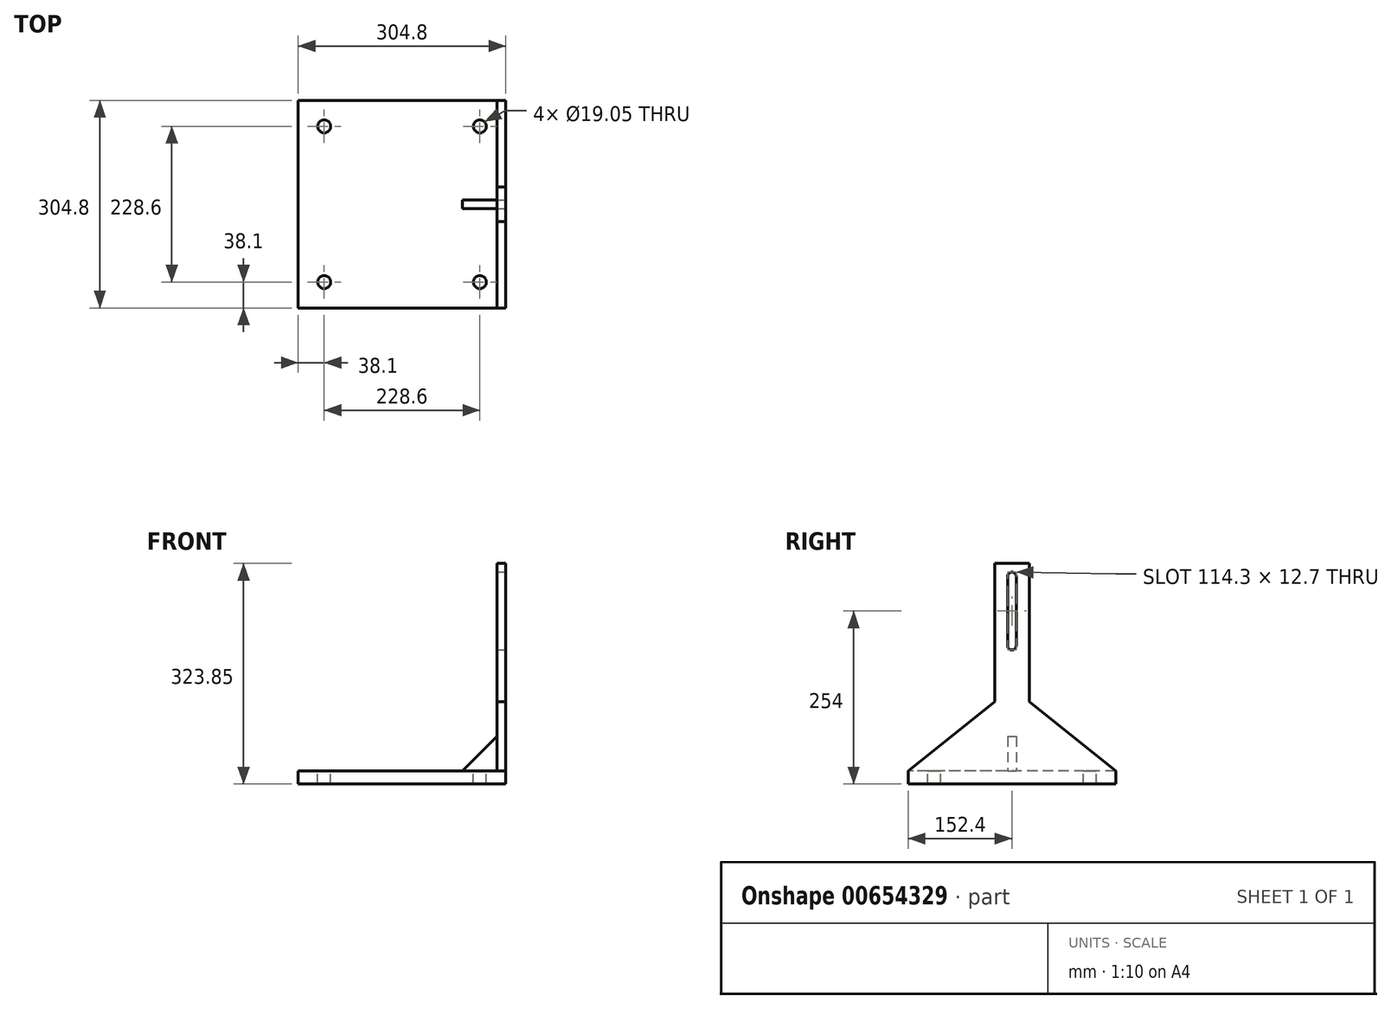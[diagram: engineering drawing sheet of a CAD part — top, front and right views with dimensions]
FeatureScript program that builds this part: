
annotation { "Feature Type Name" : "Feature", "Feature Type Description" : "" }
export const myFeature = defineFeature(function(context is Context, id is Id, definition is map)
    precondition{}
    {
        {
            var Q0;
            Q0=qCreatedBy(makeId("Top.planeOp"),FACE);
            var sketch = newSketch(context, id + "F0", { "sketchPlane" : qUnion([Q0])});
            skLineSegment(sketch, "E0.bottom", {"start": v(152.4, 152.4) * mm, "end": v(-152.4, 152.4) * mm});
            skLineSegment(sketch, "E0.top", {"start": v(152.4, -152.4) * mm, "end": v(-152.4, -152.4) * mm});
            skLineSegment(sketch, "E0.left", {"start": v(152.4, 152.4) * mm, "end": v(152.4, -152.4) * mm});
            skLineSegment(sketch, "E0.right", {"start": v(-152.4, 152.4) * mm, "end": v(-152.4, -152.4) * mm});
            skPoint(sketch, "E0.middle", {"position": v(0, 0) * mm});
            skSolve(sketch);
        }
        {
            var Q0;
            Q0 = qSketchRegion(id + "F0", true);
            extrude(context, id + "F1", {"entities" : qUnion([Q0]), "depth" : 19.05 * mm, "offsetDistance" : 25.4 * mm});
        }
        {
            var Q0;
            Q0=makeQuery(id+"F1.opExtrude","CAP_FACE",FACE,{"disambiguationData":[OSD([sQuery(id+"F0.wireOp",EDGE,"E0.bottom"),sQuery(id+"F0.wireOp",EDGE,"E0.top"),sQuery(id+"F0.wireOp",EDGE,"E0.left"),sQuery(id+"F0.wireOp",EDGE,"E0.right")])],"isStart":false});
            var sketch = newSketch(context, id + "F2", { "sketchPlane" : qUnion([Q0])});
            skLineSegment(sketch, "E1.bottom", {"start": v(152.4, 25.4) * mm, "end": v(139.7, 25.4) * mm});
            skLineSegment(sketch, "E1.top", {"start": v(152.4, -25.4) * mm, "end": v(139.7, -25.4) * mm});
            skLineSegment(sketch, "E1.left", {"start": v(152.4, 25.4) * mm, "end": v(152.4, -25.4) * mm});
            skLineSegment(sketch, "E1.right", {"start": v(139.7, 25.4) * mm, "end": v(139.7, -25.4) * mm});
            skSolve(sketch);
        }
        {
            var Q0;
            Q0 = qSketchRegion(id + "F2", true);
            extrude(context, id + "F3", {"entities" : qUnion([Q0]), "operationType" : NewBodyOperationType.ADD, "depth" : 304.8 * mm, "offsetDistance" : 25.4 * mm});
        }
        {
            var Q0;
            Q0=makeQuery(id+"F3.boolean.opBoolean","MERGE",FACE,{"derivedFrom":[makeQuery(id+"F1.opExtrude","SWEPT_FACE",FACE,{"disambiguationData":[OSD([sQuery(id+"F0.wireOp",EDGE,"E0.left")])]}),makeQuery(id+"F3.opExtrude","SWEPT_FACE",FACE,{"disambiguationData":[OSD([sQuery(id+"F2.wireOp",EDGE,"E1.left")])]})]});
            var sketch = newSketch(context, id + "F4", { "sketchPlane" : qUnion([Q0])});
            skArc(sketch, "E2", {"start": v(6.35, 304.8) * mm, "mid": v(0, 311.15) * mm, "end": v(-6.35, 304.8) * mm});
            skPoint(sketch, "E2.centerSnap0", {"position": v(0, 323.85) * mm});
            skArc(sketch, "E3", {"start": v(-6.35, 203.2) * mm, "mid": v(0, 196.85) * mm, "end": v(6.35, 203.2) * mm});
            skLineSegment(sketch, "E4", {"start": v(-6.35, 304.8) * mm, "end": v(-6.35, 203.2) * mm});
            skLineSegment(sketch, "E5", {"start": v(6.35, 304.8) * mm, "end": v(6.35, 203.2) * mm});
            skSolve(sketch);
        }
        {
            var Q0;
            Q0 = qSketchRegion(id + "F4", true);
            extrude(context, id + "F5", {"entities" : qUnion([Q0]), "operationType" : NewBodyOperationType.REMOVE, "oppositeDirection" : true, "depth" : 25.4 * mm, "offsetDistance" : 25.4 * mm});
        }
        {
            var Q0;
            Q0=qCreatedBy(makeId("Front.planeOp"),FACE);
            var sketch = newSketch(context, id + "F6", { "sketchPlane" : qUnion([Q0])});
            skLineSegment(sketch, "E6.0", {"start": v(139.7, 69.85) * mm, "end": v(139.7, 19.05) * mm});
            skLineSegment(sketch, "E7.0", {"start": v(139.7, 19.05) * mm, "end": v(88.9, 19.05) * mm});
            skLineSegment(sketch, "E8", {"start": v(139.7, 69.85) * mm, "end": v(88.9, 19.05) * mm});
            skPoint(sketch, "E9.orphan", {"position": v(139.7, 323.85) * mm});
            skPoint(sketch, "E10.orphan", {"position": v(-152.4, 19.05) * mm});
            skPoint(sketch, "E11.orphan", {"position": v(152.4, 19.05) * mm});
            skSolve(sketch);
        }
        {
            var Q0;
            Q0 = qSketchRegion(id + "F6", true);
            extrude(context, id + "F7", {"entities" : qUnion([Q0]), "operationType" : NewBodyOperationType.ADD, "endBound" : BoundingType.SYMMETRIC, "depth" : 12.7 * mm, "offsetDistance" : 25.4 * mm});
        }
        {
            var Q0;
            Q0=makeQuery(id+"F3.boolean.opBoolean","MERGE",FACE,{"derivedFrom":[makeQuery(id+"F1.opExtrude","SWEPT_FACE",FACE,{"disambiguationData":[OSD([sQuery(id+"F0.wireOp",EDGE,"E0.left")])]}),makeQuery(id+"F3.opExtrude","SWEPT_FACE",FACE,{"disambiguationData":[OSD([sQuery(id+"F2.wireOp",EDGE,"E1.left")])]})]});
            var sketch = newSketch(context, id + "F8", { "sketchPlane" : qUnion([Q0])});
            skLineSegment(sketch, "E12", {"start": v(-152.4, 19.05) * mm, "end": v(-25.4, 19.05) * mm});
            skLineSegment(sketch, "E13", {"start": v(-25.4, 19.05) * mm, "end": v(-25.4, 120.65) * mm});
            skLineSegment(sketch, "E14", {"start": v(-25.4, 120.65) * mm, "end": v(-152.4, 19.05) * mm});
            skLineSegment(sketch, "E15", {"start": v(25.4, 120.65) * mm, "end": v(25.4, 19.05) * mm});
            skLineSegment(sketch, "E16", {"start": v(25.4, 19.05) * mm, "end": v(152.4, 19.05) * mm});
            skLineSegment(sketch, "E17", {"start": v(152.4, 19.05) * mm, "end": v(25.4, 120.65) * mm});
            skSolve(sketch);
        }
        {
            var Q0;
            Q0 = qSketchRegion(id + "F8", true);
            extrude(context, id + "F9", {"entities" : qUnion([Q0]), "operationType" : NewBodyOperationType.ADD, "oppositeDirection" : true, "depth" : 12.7 * mm, "offsetDistance" : 25.4 * mm});
        }
        {
            var Q0;
            Q0=makeQuery(id+"F1.opExtrude","CAP_FACE",FACE,{"disambiguationData":[OSD([sQuery(id+"F0.wireOp",EDGE,"E0.bottom"),sQuery(id+"F0.wireOp",EDGE,"E0.top"),sQuery(id+"F0.wireOp",EDGE,"E0.left"),sQuery(id+"F0.wireOp",EDGE,"E0.right")])],"isStart":false});
            var sketch = newSketch(context, id + "F10", { "sketchPlane" : qUnion([Q0])});
            skCircle(sketch, "E18", {"center": v(-114.3, 114.3) * mm, "radius": 9.53 * mm});
            skCircle(sketch, "E19", {"center": v(114.3, 114.3) * mm, "radius": 9.53 * mm});
            skCircle(sketch, "E20", {"center": v(114.3, -114.3) * mm, "radius": 9.53 * mm});
            skCircle(sketch, "E21", {"center": v(-114.3, -114.3) * mm, "radius": 9.53 * mm});
            skSolve(sketch);
        }
        {
            var Q0;
            Q0 = qSketchRegion(id + "F10", true);
            extrude(context, id + "F11", {"entities" : qUnion([Q0]), "operationType" : NewBodyOperationType.REMOVE, "oppositeDirection" : true, "depth" : 25.4 * mm, "offsetDistance" : 25.4 * mm});
        }
    });
